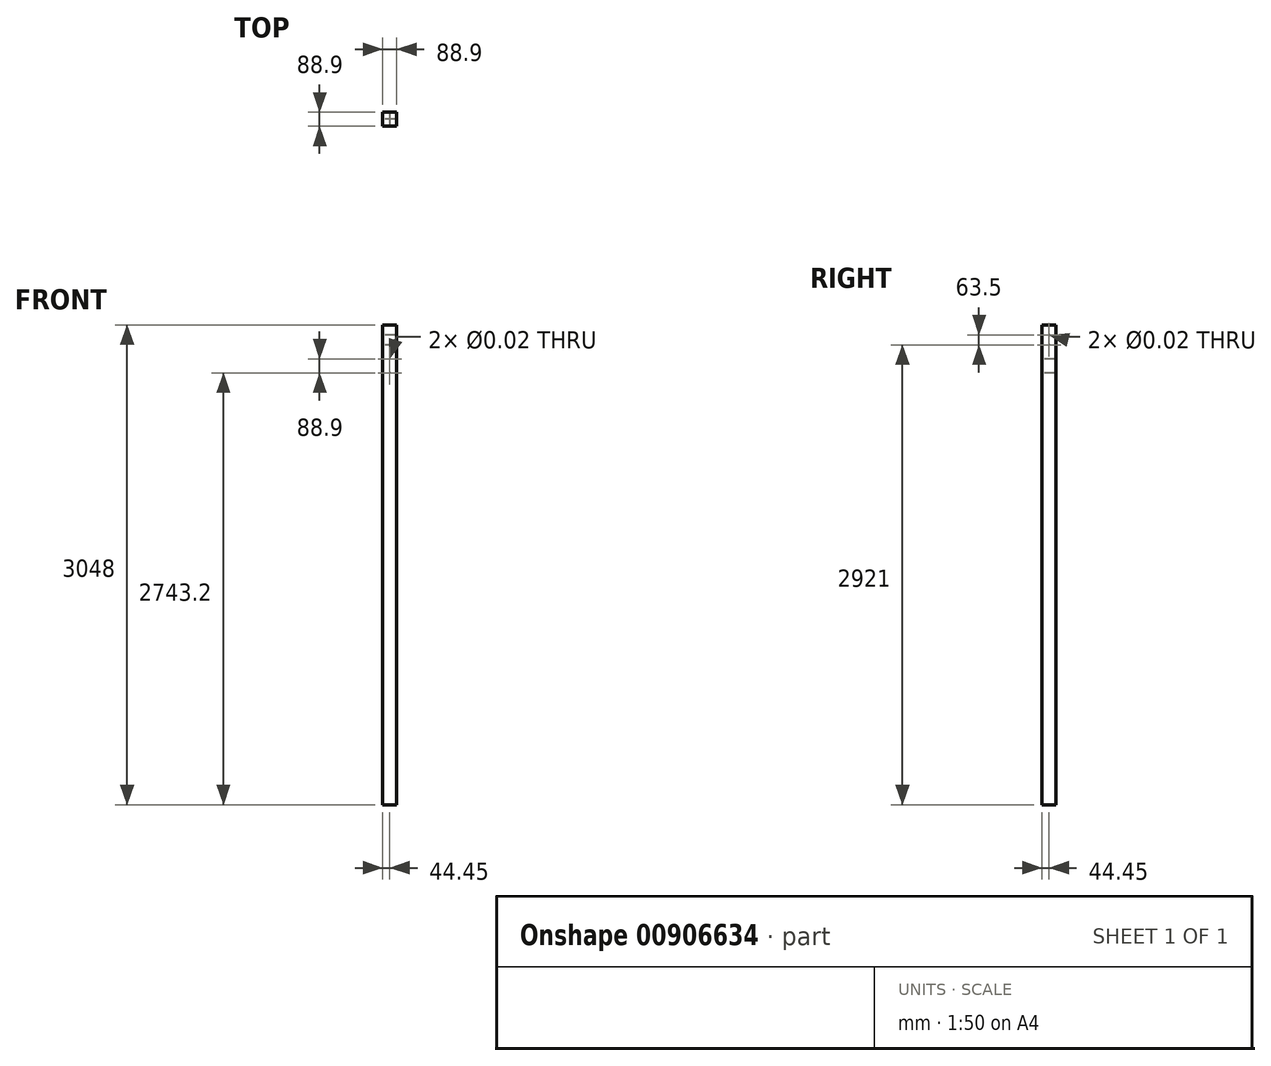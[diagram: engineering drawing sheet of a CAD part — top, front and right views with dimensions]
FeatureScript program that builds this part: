
annotation { "Feature Type Name" : "Feature", "Feature Type Description" : "" }
export const myFeature = defineFeature(function(context is Context, id is Id, definition is map)
    precondition{}
    {
        {
            var Q0;
            Q0=qCreatedBy(makeId("Front.planeOp"),FACE);
            var sketch = newSketch(context, id + "F0", { "sketchPlane" : qUnion([Q0])});
            skLineSegment(sketch, "E0", {"start": v(0, 0) * mm, "end": v(0, -3048) * mm});
            skLineSegment(sketch, "E1", {"start": v(0, -3048) * mm, "end": v(88.9, -3048) * mm});
            skLineSegment(sketch, "E2", {"start": v(88.9, -3048) * mm, "end": v(88.9, 0) * mm});
            skLineSegment(sketch, "E3", {"start": v(88.9, 0) * mm, "end": v(0, 0) * mm});
            skSolve(sketch);
        }
        {
            var Q0;
            Q0=makeQuery(id+"F0.imprint","IMPRINT",FACE,{"disambiguationData":[TD([[makeQuery(id+"F0.imprint","IMPRINT",EDGE,{"derivedFrom":sQuery(id+"F0.wireOp",EDGE,"E0")}),1.0]])]});
            extrude(context, id + "F1", {"entities" : qUnion([Q0]), "depth" : 88.9 * mm, "offsetDistance" : 25.4 * mm});
        }
        {
            var Q0;
            Q0=makeQuery(id+"F1.opExtrude","CAP_FACE",FACE,{"disambiguationData":[OSD([sQuery(id+"F0.wireOp",EDGE,"E0"),sQuery(id+"F0.wireOp",EDGE,"E1"),sQuery(id+"F0.wireOp",EDGE,"E2"),sQuery(id+"F0.wireOp",EDGE,"E3")])],"isStart":false});
            var sketch = newSketch(context, id + "F2", { "sketchPlane" : qUnion([Q0])});
            skLineSegment(sketch, "E4", {"start": v(44.45, 0) * mm, "end": v(44.45, -139.7) * mm});
            skLineSegment(sketch, "E5", {"start": v(44.45, -139.7) * mm, "end": v(44.45, -381) * mm});
            skLineSegment(sketch, "E6", {"start": v(44.45, -139.7) * mm, "end": v(-70.27, -139.7) * mm});
            skLineSegment(sketch, "E7", {"start": v(-70.27, -139.7) * mm, "end": v(-70.27, -215.9) * mm});
            skLineSegment(sketch, "E8", {"start": v(-70.27, -215.9) * mm, "end": v(-70.27, -304.8) * mm});
            skLineSegment(sketch, "E9", {"start": v(-70.27, -304.8) * mm, "end": v(72.23, -304.8) * mm});
            skLineSegment(sketch, "E10", {"start": v(-70.27, -215.9) * mm, "end": v(67.3, -215.9) * mm});
            skLineSegment(sketch, "E11", {"start": v(0, 0) * mm, "end": v(-63.22, 0) * mm});
            skLineSegment(sketch, "E12", {"start": v(-63.22, 0) * mm, "end": v(-63.22, -38.1) * mm});
            skLineSegment(sketch, "E13", {"start": v(-63.22, -38.1) * mm, "end": v(-63.22, -101.6) * mm});
            skLineSegment(sketch, "E14", {"start": v(-63.22, -101.6) * mm, "end": v(63.77, -101.6) * mm});
            skLineSegment(sketch, "E15", {"start": v(-63.22, -38.1) * mm, "end": v(68.7, -38.1) * mm});
            skCircle(sketch, "E16", {"center": v(44.45, -304.8) * mm, "radius": 6.35 * mm});
            skCircle(sketch, "E17", {"center": v(44.45, -215.9) * mm, "radius": 6.35 * mm});
            skCircle(sketch, "E18", {"center": v(44.45, -101.6) * mm, "radius": 6.35 * mm});
            skCircle(sketch, "E19", {"center": v(44.45, -38.1) * mm, "radius": 6.35 * mm});
            skSolve(sketch);
        }
        {
            var Q0;
            Q0=sQuery(id+"F2.wireOp",VERTEX,"E17.center");
            var Q1;
            Q1=sQuery(id+"F2.wireOp",VERTEX,"E16.center");
            var Q2;
            Q2=makeQuery(id+"F1.opExtrude","SWEPT_BODY",BODY,{"disambiguationData":[OSD([sQuery(id+"F0.wireOp",EDGE,"E0"),sQuery(id+"F0.wireOp",EDGE,"E1"),sQuery(id+"F0.wireOp",EDGE,"E2"),sQuery(id+"F0.wireOp",EDGE,"E3")])]});
            hole(context, id + "F3", {"style" : HoleStyle.SIMPLE, "endStyle" : HoleEndStyle.THROUGH, "standardTappedOrClearance" : lookupTablePath({ "standard" : "ANSI", "size" : "1/2 (0.5)", "type" : "Drilled" }), "standardBlindInLast" : lookupTablePath({ "standard" : "ANSI", "size" : "1/2", "type" : "Drilled" }), "holeDiameter" : 1 / 50.8 * mm, "majorDiameter" : 6.35 * mm, "isTappedThrough" : true, "tappedDepth" : 10.3 * mm, "tapClearance" : 3, "startFromSketch" : true, "locations" : qUnion([Q0, Q1]), "scope" : qUnion([Q2])});
        }
        {
            var Q0;
            Q0=makeQuery(id+"F1.opExtrude","SWEPT_FACE",FACE,{"disambiguationData":[OSD([sQuery(id+"F0.wireOp",EDGE,"E0")])]});
            var sketch = newSketch(context, id + "F4", { "sketchPlane" : qUnion([Q0])});
            skLineSegment(sketch, "E20", {"start": v(88.9, 0) * mm, "end": v(111.13, 0) * mm});
            skLineSegment(sketch, "E21", {"start": v(111.13, 0) * mm, "end": v(111.13, -63.5) * mm});
            skLineSegment(sketch, "E22", {"start": v(111.13, -63.5) * mm, "end": v(111.13, -127) * mm});
            skLineSegment(sketch, "E23", {"start": v(111.13, -127) * mm, "end": v(-26.3, -127) * mm});
            skLineSegment(sketch, "E24", {"start": v(111.13, -63.5) * mm, "end": v(-38.27, -63.5) * mm});
            skLineSegment(sketch, "E25", {"start": v(44.45, 0) * mm, "end": v(44.45, -164.36) * mm});
            skCircle(sketch, "E26", {"center": v(44.45, -63.5) * mm, "radius": 6.35 * mm});
            skCircle(sketch, "E27", {"center": v(44.45, -127) * mm, "radius": 6.35 * mm});
            skSolve(sketch);
        }
        {
            var Q0;
            Q0=sQuery(id+"F4.wireOp",VERTEX,"E26.center");
            var Q1;
            Q1=sQuery(id+"F4.wireOp",VERTEX,"E27.center");
            var Q2;
            Q2=makeQuery(id+"F1.opExtrude","SWEPT_BODY",BODY,{"disambiguationData":[OSD([sQuery(id+"F0.wireOp",EDGE,"E0"),sQuery(id+"F0.wireOp",EDGE,"E1"),sQuery(id+"F0.wireOp",EDGE,"E2"),sQuery(id+"F0.wireOp",EDGE,"E3")])]});
            hole(context, id + "F5", {"style" : HoleStyle.SIMPLE, "endStyle" : HoleEndStyle.THROUGH, "standardTappedOrClearance" : lookupTablePath({ "standard" : "ANSI", "size" : "1/2 (0.5)", "type" : "Drilled" }), "standardBlindInLast" : lookupTablePath({ "standard" : "ANSI", "size" : "1/2", "type" : "Drilled" }), "holeDiameter" : 1 / 50.8 * mm, "majorDiameter" : 6.35 * mm, "isTappedThrough" : true, "tappedDepth" : 10.3 * mm, "tapClearance" : 3, "startFromSketch" : true, "locations" : qUnion([Q0, Q1]), "scope" : qUnion([Q2])});
        }
    });
